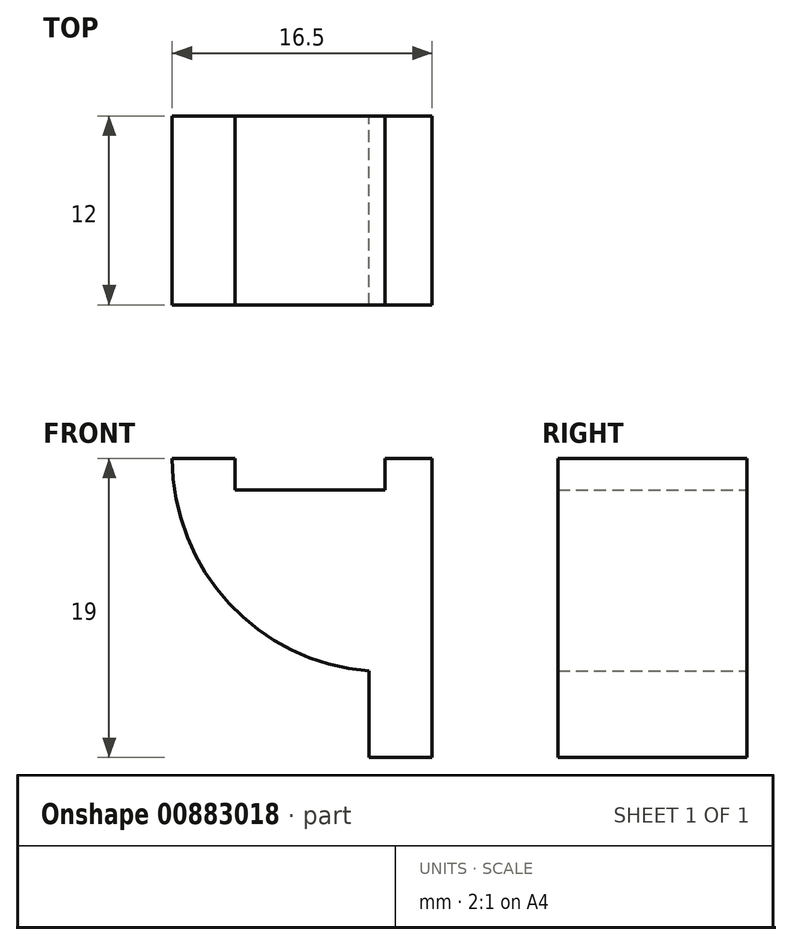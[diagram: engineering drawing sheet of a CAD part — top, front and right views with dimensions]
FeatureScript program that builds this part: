
annotation { "Feature Type Name" : "Feature", "Feature Type Description" : "" }
export const myFeature = defineFeature(function(context is Context, id is Id, definition is map)
    precondition{}
    {
        {
            var Q0;
            Q0=qCreatedBy(makeId("Front.planeOp"),FACE);
            var sketch = newSketch(context, id + "F0", { "sketchPlane" : qUnion([Q0])});
            skLineSegment(sketch, "E0.bottom", {"start": v(0, 9.5) * mm, "end": v(3, 9.5) * mm});
            skLineSegment(sketch, "E0.top", {"start": v(0, -9.5) * mm, "end": v(3, -9.5) * mm});
            skLineSegment(sketch, "E0.left", {"start": v(0, 9.5) * mm, "end": v(0, -9.5) * mm});
            skLineSegment(sketch, "E0.right", {"start": v(3, 9.5) * mm, "end": v(3, -9.5) * mm});
            skLineSegment(sketch, "E1", {"start": v(0, -9.5) * mm, "end": v(-1, -9.5) * mm});
            skLineSegment(sketch, "E2", {"start": v(-1, -9.5) * mm, "end": v(-1, -4) * mm});
            skLineSegment(sketch, "E3", {"start": v(0, 9.5) * mm, "end": v(0, 7.5) * mm, "construction": true});
            skLineSegment(sketch, "E4", {"start": v(0, 7.5) * mm, "end": v(-9.5, 7.5) * mm});
            skLineSegment(sketch, "E5", {"start": v(-9.5, 7.5) * mm, "end": v(-9.5, 9.5) * mm});
            skLineSegment(sketch, "E6", {"start": v(-9.5, 9.5) * mm, "end": v(-13.5, 9.5) * mm});
            skPoint(sketch, "E7.third.point", {"position": v(18.17, 13.18) * mm});
            skLineSegment(sketch, "E8", {"start": v(-13.5, 9.5) * mm, "end": v(-13.5, -4) * mm, "construction": true});
            skLineSegment(sketch, "E9", {"start": v(-13.5, -4) * mm, "end": v(-1, -4) * mm, "construction": true});
            skArc(sketch, "E10", {"start": v(-13.5, 9.5) * mm, "mid": v(-9.9, 0.3) * mm, "end": v(-1, -4) * mm});
            skSolve(sketch);
        }
        {
            var Q0;
            {var subQ1=sQuery(id+"F0.wireOp",EDGE,"E1");Q0=makeQuery(id+"F0.imprint","IMPRINT",FACE,{"disambiguationData":[TD([[makeQuery(id+"F0.imprint","IMPRINT",EDGE,{"derivedFrom":subQ1}),-1.0]])]});}
            var Q1;
            {var subQ3=sQuery(id+"F0.wireOp",EDGE,"E0.bottom");Q1=makeQuery(id+"F0.imprint","IMPRINT",FACE,{"disambiguationData":[TD([[makeQuery(id+"F0.imprint","IMPRINT",EDGE,{"derivedFrom":subQ3}),-1.0]])]});}
            extrude(context, id + "F1", {"entities" : qUnion([Q0, Q1]), "depth" : 12 * mm, "offsetDistance" : 25 * mm});
        }
    });
